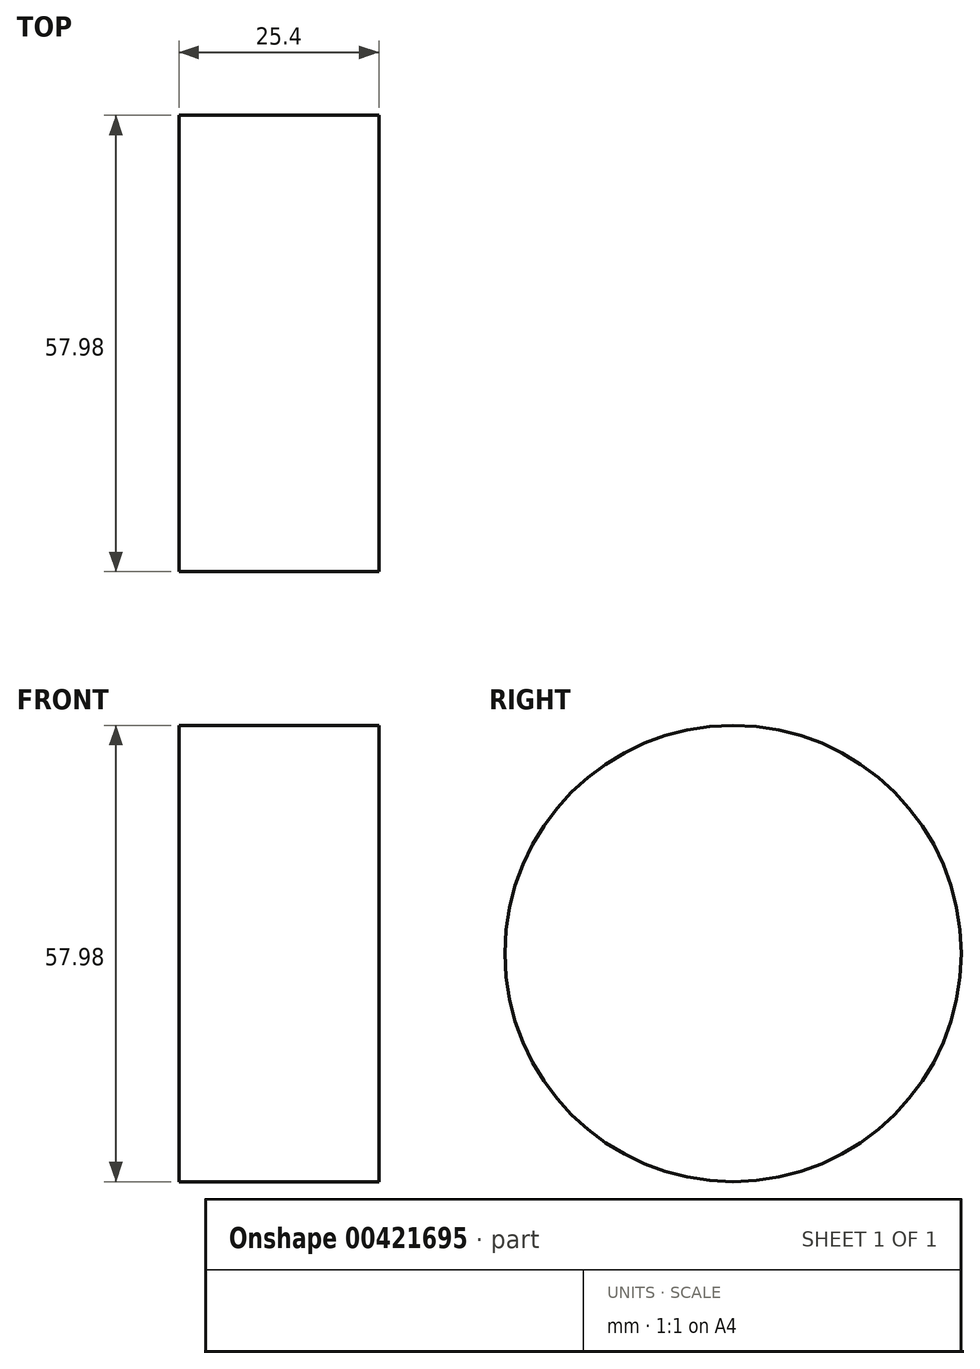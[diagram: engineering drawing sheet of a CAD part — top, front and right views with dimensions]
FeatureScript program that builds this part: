
annotation { "Feature Type Name" : "Feature", "Feature Type Description" : "" }
export const myFeature = defineFeature(function(context is Context, id is Id, definition is map)
    precondition{}
    {
        {
            var Q0;
            Q0=qCreatedBy(makeId("Right.planeOp"),FACE);
            var sketch = newSketch(context, id + "F0", { "sketchPlane" : qUnion([Q0])});
            skCircle(sketch, "E0", {"center": v(0, 0) * mm, "radius": 28.99 * mm});
            skSolve(sketch);
        }
        {
            var Q0;
            Q0 = qSketchRegion(id + "F0", true);
            extrude(context, id + "F1", {"entities" : qUnion([Q0]), "depth" : 25.4 * mm});
        }
    });
